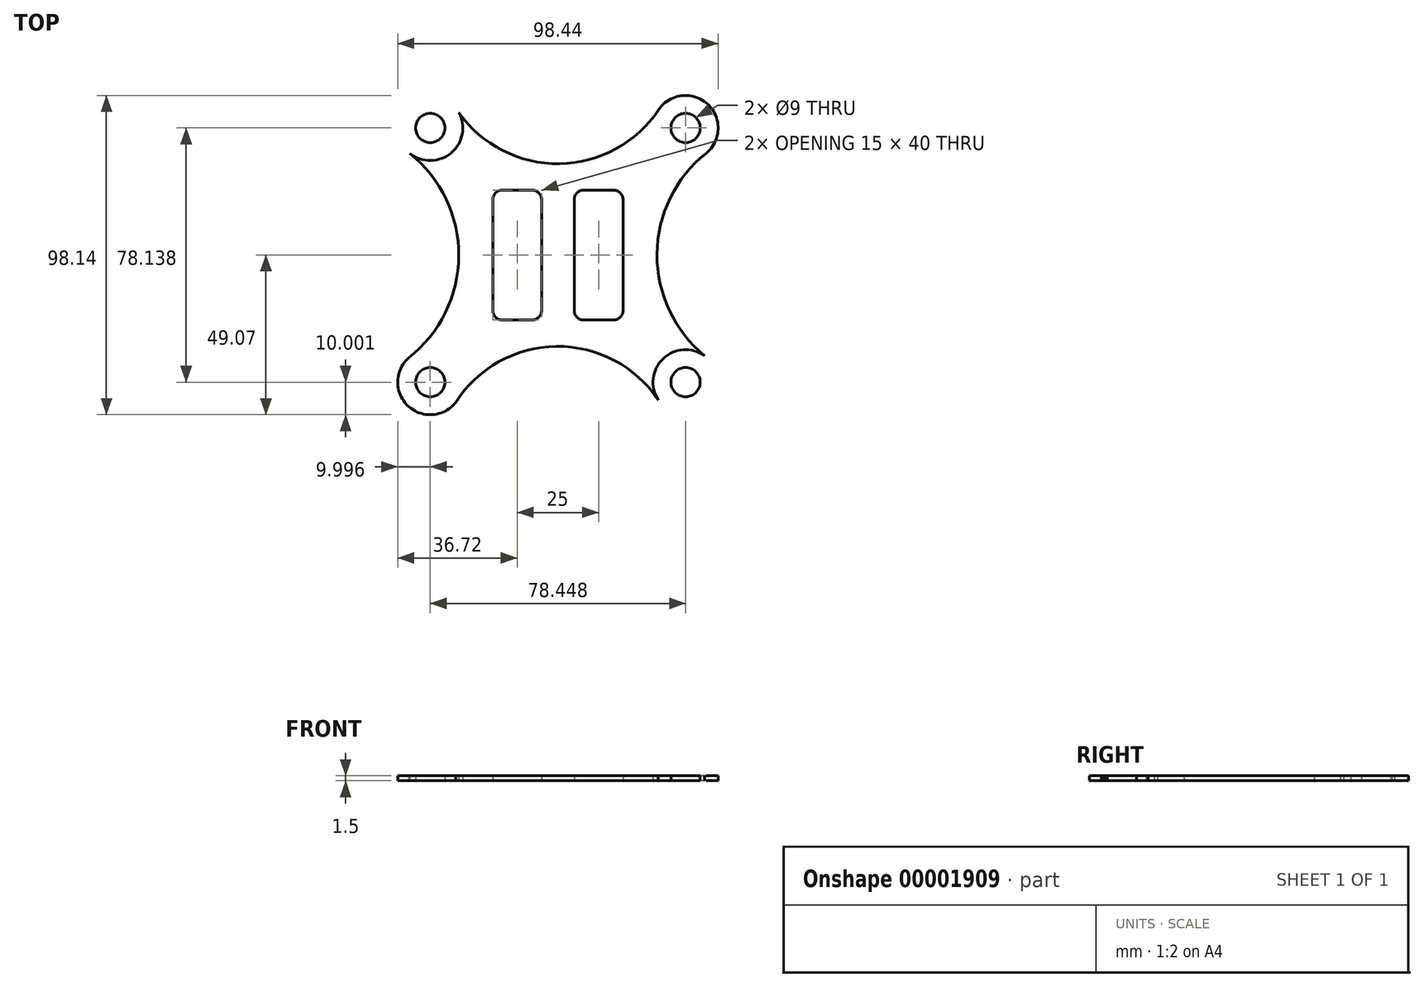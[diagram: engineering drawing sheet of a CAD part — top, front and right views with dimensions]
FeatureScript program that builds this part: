
annotation { "Feature Type Name" : "Feature", "Feature Type Description" : "" }
export const myFeature = defineFeature(function(context is Context, id is Id, definition is map)
    precondition{}
    {
        {
            var Q0;
            Q0=qCreatedBy(makeId("Top.planeOp"),FACE);
            var sketch = newSketch(context, id + "F0", { "sketchPlane" : qUnion([Q0])});
            skPoint(sketch, "E0.rect.middle", {"position": v(0, 0) * mm});
            skCircle(sketch, "E1", {"center": v(39.22, 39.07) * mm, "radius": 4.5 * mm});
            skLineSegment(sketch, "E2", {"start": v(-49, 0) * mm, "end": v(49, 0) * mm, "construction": true});
            skLineSegment(sketch, "E3", {"start": v(0, -49) * mm, "end": v(0, 49) * mm, "construction": true});
            skCircle(sketch, "E4.0.MirrorC", {"center": v(39.22, -39.07) * mm, "radius": 4.5 * mm});
            skCircle(sketch, "E5.0.MirrorC", {"center": v(-39.22, 39.07) * mm, "radius": 4.5 * mm});
            skCircle(sketch, "E6.0.MirrorC", {"center": v(-39.22, -39.07) * mm, "radius": 4.5 * mm});
            skPoint(sketch, "E7.visualSharp", {"position": v(49, 49) * mm});
            skPoint(sketch, "E8.visualSharp", {"position": v(-49, 49) * mm});
            skPoint(sketch, "E9.visualSharp", {"position": v(-49, -49) * mm});
            skPoint(sketch, "E10.visualSharp", {"position": v(49, -49) * mm});
            skLineSegment(sketch, "E11.rect.bottom", {"start": v(-8, -20) * mm, "end": v(-17, -20) * mm});
            skLineSegment(sketch, "E11.rect.top", {"start": v(-8, 20) * mm, "end": v(-17, 20) * mm});
            skLineSegment(sketch, "E11.rect.right", {"start": v(-20, -17) * mm, "end": v(-20, 17) * mm});
            skCircle(sketch, "E12.0.MirrorC", {"center": v(39.22, -39.07) * mm, "radius": 10 * mm});
            skCircle(sketch, "E13.0.MirrorC", {"center": v(-39.22, -39.07) * mm, "radius": 10 * mm});
            skCircle(sketch, "E13.1.MirrorC", {"center": v(-39.22, 39.07) * mm, "radius": 10 * mm});
            skArc(sketch, "E14", {"start": v(45.5, 31.29) * mm, "mid": v(30.46, -0.25) * mm, "end": v(45.88, -31.6) * mm});
            skArc(sketch, "E15.0.MirrorCS", {"start": v(-45.5, 31.29) * mm, "mid": v(-30.46, -0.25) * mm, "end": v(-45.88, -31.6) * mm});
            skArc(sketch, "E16", {"start": v(-31.44, 45.34) * mm, "mid": v(-0.4, 28.08) * mm, "end": v(30.97, 44.72) * mm});
            skArc(sketch, "E17.0.MirrorCS", {"start": v(-31.44, -45.34) * mm, "mid": v(-0.4, -28.08) * mm, "end": v(30.97, -44.72) * mm});
            skCircle(sketch, "E18.0.MirrorC", {"center": v(39.22, 39.07) * mm, "radius": 10 * mm});
            skLineSegment(sketch, "E19.rect.right", {"start": v(-5, -17) * mm, "end": v(-5, 17) * mm});
            skPoint(sketch, "E20.newPointA", {"position": v(20, 20) * mm});
            skPoint(sketch, "E20.newPointB", {"position": v(-5, 20) * mm});
            skArc(sketch, "E20.filletArc", {"start": v(-5, 17) * mm, "mid": v(-5.88, 19.12) * mm, "end": v(-8, 20) * mm});
            skPoint(sketch, "E21.newPointA", {"position": v(20, -20) * mm});
            skPoint(sketch, "E21.newPointB", {"position": v(-5, -20) * mm});
            skArc(sketch, "E21.filletArc", {"start": v(-8, -20) * mm, "mid": v(-5.88, -19.12) * mm, "end": v(-5, -17) * mm});
            skPoint(sketch, "E22.visualSharp", {"position": v(-20, 20) * mm});
            skArc(sketch, "E22.filletArc", {"start": v(-17, 20) * mm, "mid": v(-19.12, 19.12) * mm, "end": v(-20, 17) * mm});
            skPoint(sketch, "E23.visualSharp", {"position": v(-20, -20) * mm});
            skArc(sketch, "E23.filletArc", {"start": v(-20, -17) * mm, "mid": v(-19.12, -19.12) * mm, "end": v(-17, -20) * mm});
            skArc(sketch, "E24.0.MirrorCS", {"start": v(8, -20) * mm, "mid": v(5.88, -19.12) * mm, "end": v(5, -17) * mm});
            skLineSegment(sketch, "E24.1.MirrorCS", {"start": v(8, 20) * mm, "end": v(17, 20) * mm});
            skLineSegment(sketch, "E24.2.MirrorCS", {"start": v(8, -20) * mm, "end": v(17, -20) * mm});
            skArc(sketch, "E24.3.MirrorCS", {"start": v(20, -17) * mm, "mid": v(19.12, -19.12) * mm, "end": v(17, -20) * mm});
            skArc(sketch, "E24.4.MirrorCS", {"start": v(5, 17) * mm, "mid": v(5.88, 19.12) * mm, "end": v(8, 20) * mm});
            skArc(sketch, "E24.5.MirrorCS", {"start": v(17, 20) * mm, "mid": v(19.12, 19.12) * mm, "end": v(20, 17) * mm});
            skLineSegment(sketch, "E25.0.MirrorCS", {"start": v(20, -17) * mm, "end": v(20, 17) * mm});
            skLineSegment(sketch, "E25.1.MirrorCS", {"start": v(5, -17) * mm, "end": v(5, 17) * mm});
            skSolve(sketch);
        }
        {
            var Q0;
            Q0=makeQuery(id+"F0.imprint","IMPRINT",FACE,{"disambiguationData":[TD([[makeQuery(id+"F0.imprint","IMPRINT",EDGE,{"derivedFrom":sQuery(id+"F0.wireOp",EDGE,"E11.rect.bottom")}),1.0]])]});
            extrude(context, id + "F1", {"entities" : qUnion([Q0]), "depth" : 1.5 * mm});
        }
        {
            var Q0;
            Q0=makeQuery(id+"F0.imprint","IMPRINT",FACE,{"disambiguationData":[TD([[makeQuery(id+"F0.imprint","IMPRINT",EDGE,{"derivedFrom":sQuery(id+"F0.wireOp",EDGE,"E5.0.MirrorC")}),1.0]])]});
            var Q1;
            Q1=makeQuery(id+"F0.imprint","IMPRINT",FACE,{"disambiguationData":[TD([[makeQuery(id+"F0.imprint","IMPRINT",EDGE,{"derivedFrom":sQuery(id+"F0.wireOp",EDGE,"E1")}),-1.0]])]});
            var Q2;
            Q2=makeQuery(id+"F0.imprint","IMPRINT",FACE,{"disambiguationData":[TD([[makeQuery(id+"F0.imprint","IMPRINT",EDGE,{"derivedFrom":sQuery(id+"F0.wireOp",EDGE,"E4.0.MirrorC")}),1.0]])]});
            var Q3;
            Q3=makeQuery(id+"F0.imprint","IMPRINT",FACE,{"disambiguationData":[TD([[makeQuery(id+"F0.imprint","IMPRINT",EDGE,{"derivedFrom":sQuery(id+"F0.wireOp",EDGE,"E6.0.MirrorC")}),-1.0]])]});
            extrude(context, id + "F2", {"entities" : qUnion([Q0, Q1, Q2, Q3]), "operationType" : NewBodyOperationType.ADD, "depth" : 1.5 * mm});
        }
    });
